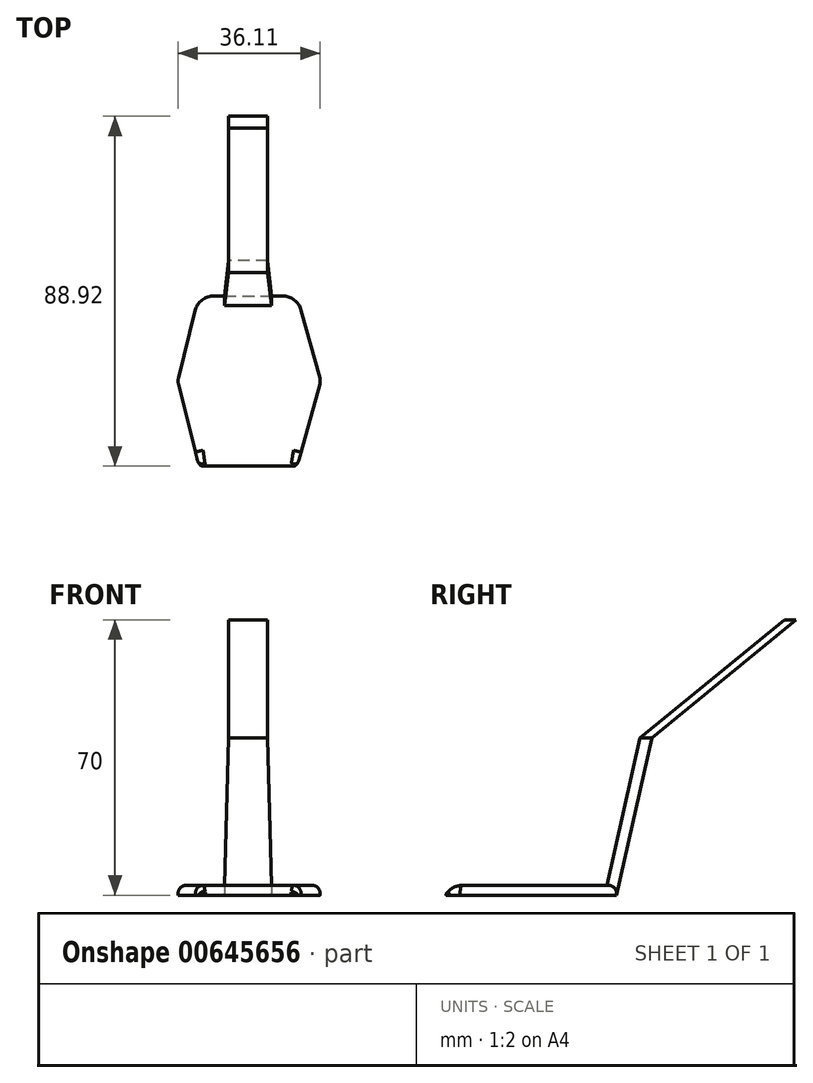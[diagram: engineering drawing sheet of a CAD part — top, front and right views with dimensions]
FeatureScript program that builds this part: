
annotation { "Feature Type Name" : "Feature", "Feature Type Description" : "" }
export const myFeature = defineFeature(function(context is Context, id is Id, definition is map)
    precondition{}
    {
        {
            var Q0;
            Q0=qCreatedBy(makeId("Top.planeOp"),FACE);
            var sketch = newSketch(context, id + "F0", { "sketchPlane" : qUnion([Q0])});
            skLineSegment(sketch, "E0.0", {"start": v(-12.5, 21.65) * mm, "end": v(12.5, 21.65) * mm});
            skLineSegment(sketch, "E0.1", {"start": v(12.5, 21.65) * mm, "end": v(18.43, 0) * mm});
            skLineSegment(sketch, "E0.2", {"start": v(18.43, 0) * mm, "end": v(12.5, -21.65) * mm});
            skLineSegment(sketch, "E0.3", {"start": v(12.5, -21.65) * mm, "end": v(-12.5, -21.65) * mm});
            skLineSegment(sketch, "E0.4", {"start": v(-12.5, -21.65) * mm, "end": v(-17.89, 0) * mm});
            skLineSegment(sketch, "E0.5", {"start": v(-17.89, 0) * mm, "end": v(-12.5, 21.65) * mm});
            skPoint(sketch, "E0.0.midPoint", {"position": v(0, 21.65) * mm});
            skSolve(sketch);
        }
        {
            var Q0;
            Q0 = qSketchRegion(id + "F0", true);
            extrude(context, id + "F1", {"entities" : qUnion([Q0]), "depth" : 2.5 * mm, "offsetDistance" : 25 * mm});
        }
        {
            var Q0;
            Q0=qCreatedBy(makeId("Top.planeOp"),FACE);
            cPlane(context, id + "F2", {"entities" : qUnion([Q0]), "cplaneType" : CPlaneType.OFFSET, "offset" : 40 * mm, "width" : 150 * mm, "height" : 150 * mm});
        }
        {
            var Q0;
            Q0=qCreatedBy(id+"F2.planeOp",FACE);
            var sketch = newSketch(context, id + "F3", { "sketchPlane" : qUnion([Q0])});
            skLineSegment(sketch, "E1.bottom", {"start": v(5, 27.57) * mm, "end": v(-5, 27.57) * mm});
            skLineSegment(sketch, "E1.top", {"start": v(5, 30.57) * mm, "end": v(-5, 30.57) * mm});
            skLineSegment(sketch, "E1.left", {"start": v(5, 27.57) * mm, "end": v(5, 30.57) * mm});
            skLineSegment(sketch, "E1.right", {"start": v(-5, 27.57) * mm, "end": v(-5, 30.57) * mm});
            skPoint(sketch, "E1.middle", {"position": v(0, 29.07) * mm});
            skSolve(sketch);
        }
        {
            var Q0;
            Q0=makeQuery(id+"F1.opExtrude","CAP_FACE",FACE,{"disambiguationData":[OSD([sQuery(id+"F0.wireOp",EDGE,"E0.0"),sQuery(id+"F0.wireOp",EDGE,"E0.1"),sQuery(id+"F0.wireOp",EDGE,"E0.2"),sQuery(id+"F0.wireOp",EDGE,"E0.3"),sQuery(id+"F0.wireOp",EDGE,"E0.4"),sQuery(id+"F0.wireOp",EDGE,"E0.5")])],"isStart":true});
            var sketch = newSketch(context, id + "F4", { "sketchPlane" : qUnion([Q0])});
            skLineSegment(sketch, "E2.bottom", {"start": v(6, -21.65) * mm, "end": v(-6, -21.65) * mm});
            skLineSegment(sketch, "E2.top", {"start": v(6, -18.65) * mm, "end": v(-6, -18.65) * mm});
            skLineSegment(sketch, "E2.left", {"start": v(6, -21.65) * mm, "end": v(6, -18.65) * mm});
            skLineSegment(sketch, "E2.right", {"start": v(-6, -21.65) * mm, "end": v(-6, -18.65) * mm});
            skPoint(sketch, "E2.middle", {"position": v(0, -20.15) * mm});
            skSolve(sketch);
        }
        {
            var Q1;
            Q1=makeQuery(id+"F4.imprint","IMPRINT",FACE,{"disambiguationData":[TD([[makeQuery(id+"F4.imprint","IMPRINT",EDGE,{"derivedFrom":sQuery(id+"F4.wireOp",EDGE,"E2.bottom")}),1.0]])]});
            var Q2;
            Q2=makeQuery(id+"F3.imprint","IMPRINT",FACE,{"disambiguationData":[TD([[makeQuery(id+"F3.imprint","IMPRINT",EDGE,{"derivedFrom":sQuery(id+"F3.wireOp",EDGE,"E1.bottom")}),-1.0]])]});
            loft(context, id + "F5", {"operationType" : NewBodyOperationType.ADD, "sheetProfilesArray" : [{ "sheetProfileEntities" : qUnion([Q1]) }, { "sheetProfileEntities" : qUnion([Q2]) }]});
        }
        {
            var Q0;
            Q0=qCreatedBy(id+"F2.planeOp",FACE);
            cPlane(context, id + "F6", {"entities" : qUnion([Q0]), "cplaneType" : CPlaneType.OFFSET, "offset" : 30 * mm, "width" : 150 * mm, "height" : 150 * mm});
        }
        {
            var Q0;
            Q0=qCreatedBy(id+"F6.planeOp",FACE);
            var sketch = newSketch(context, id + "F7", { "sketchPlane" : qUnion([Q0])});
            skLineSegment(sketch, "E3.bottom", {"start": v(5, 64.27) * mm, "end": v(-5, 64.27) * mm});
            skLineSegment(sketch, "E3.top", {"start": v(5, 67.27) * mm, "end": v(-5, 67.27) * mm});
            skLineSegment(sketch, "E3.left", {"start": v(5, 64.27) * mm, "end": v(5, 67.27) * mm});
            skLineSegment(sketch, "E3.right", {"start": v(-5, 64.27) * mm, "end": v(-5, 67.27) * mm});
            skPoint(sketch, "E3.middle", {"position": v(0, 65.77) * mm});
            skSolve(sketch);
        }
        {
            var Q1;
            Q1=makeQuery(id+"F5.opLoft","CAP_FACE",FACE,{"disambiguationData":[OSD([makeQuery(id+"F3.imprint","IMPRINT",FACE,{"disambiguationData":[TD([[makeQuery(id+"F3.imprint","IMPRINT",EDGE,{"derivedFrom":sQuery(id+"F3.wireOp",EDGE,"E1.bottom")}),-1.0]])]})])],"isStart":true});
            var Q2;
            Q2=makeQuery(id+"F7.imprint","IMPRINT",FACE,{"disambiguationData":[TD([[makeQuery(id+"F7.imprint","IMPRINT",EDGE,{"derivedFrom":sQuery(id+"F7.wireOp",EDGE,"E3.bottom")}),-1.0]])]});
            loft(context, id + "F8", {"operationType" : NewBodyOperationType.ADD, "sheetProfilesArray" : [{ "sheetProfileEntities" : qUnion([Q1]) }, { "sheetProfileEntities" : qUnion([Q2]) }]});
        }
        {
            var Q0;
            Q0=makeQuery(id+"F1.opExtrude","CAP_EDGE",EDGE,{"disambiguationData":[OSD([sQuery(id+"F0.wireOp",EDGE,"E0.3")])],"isStart":false});
            chamfer(context, id + "F9", {"entities" : qUnion([Q0]), "width" : 2 * mm, "tangentPropagation" : true});
        }
        {
            var Q0;
            {var subQ0=sQuery(id+"F0.wireOp",EDGE,"E0.3");Q0=makeQuery(id+"F9.opChamfer","BLEND_EDGE",EDGE,{"blendedFrom":[makeQuery(id+"F1.opExtrude","CAP_EDGE",EDGE,{"disambiguationData":[OSD([subQ0])],"isStart":false}),makeQuery(id+"F1.opExtrude","CAP_FACE",FACE,{"disambiguationData":[OSD([sQuery(id+"F0.wireOp",EDGE,"E0.0"),sQuery(id+"F0.wireOp",EDGE,"E0.1"),sQuery(id+"F0.wireOp",EDGE,"E0.2"),subQ0,sQuery(id+"F0.wireOp",EDGE,"E0.4"),sQuery(id+"F0.wireOp",EDGE,"E0.5")])],"isStart":false})],"blendedInto":[makeQuery(id+"F1.opExtrude","CAP_FACE",FACE,{"disambiguationData":[OSD([sQuery(id+"F0.wireOp",EDGE,"E0.0"),sQuery(id+"F0.wireOp",EDGE,"E0.1"),sQuery(id+"F0.wireOp",EDGE,"E0.2"),subQ0,sQuery(id+"F0.wireOp",EDGE,"E0.4"),sQuery(id+"F0.wireOp",EDGE,"E0.5")])],"isStart":false})]});}
            fillet(context, id + "F10", {"entities" : qUnion([Q0]), "radius" : 5 * mm, "tangentPropagation" : true, "allowEdgeOverflow" : false});
        }
        {
            var Q0;
            Q0=makeQuery(id+"F1.opExtrude","SWEPT_EDGE",EDGE,{"disambiguationData":[OSD([sQuery(id+"F0.wireOp",EDGE,"E0.0"),sQuery(id+"F0.wireOp",EDGE,"E0.5")])]});
            var Q1;
            Q1=makeQuery(id+"F1.opExtrude","SWEPT_EDGE",EDGE,{"disambiguationData":[OSD([sQuery(id+"F0.wireOp",EDGE,"E0.0"),sQuery(id+"F0.wireOp",EDGE,"E0.1")])]});
            fillet(context, id + "F11", {"entities" : qUnion([Q0, Q1]), "radius" : 5 * mm, "tangentPropagation" : true, "allowEdgeOverflow" : false});
        }
        {
            var Q0;
            Q0=makeQuery(id+"F1.opExtrude","SWEPT_EDGE",EDGE,{"disambiguationData":[OSD([sQuery(id+"F0.wireOp",EDGE,"E0.4"),sQuery(id+"F0.wireOp",EDGE,"E0.5")])]});
            var Q1;
            Q1=makeQuery(id+"F1.opExtrude","SWEPT_EDGE",EDGE,{"disambiguationData":[OSD([sQuery(id+"F0.wireOp",EDGE,"E0.1"),sQuery(id+"F0.wireOp",EDGE,"E0.2")])]});
            fillet(context, id + "F12", {"entities" : qUnion([Q0, Q1]), "radius" : 3 * mm, "tangentPropagation" : true, "allowEdgeOverflow" : false});
        }
        {
            var Q0;
            Q0=makeQuery(id+"F1.opExtrude","CAP_EDGE",EDGE,{"disambiguationData":[OSD([sQuery(id+"F0.wireOp",EDGE,"E0.2")])],"isStart":false});
            var Q1;
            Q1=makeQuery(id+"F1.opExtrude","CAP_EDGE",EDGE,{"disambiguationData":[OSD([sQuery(id+"F0.wireOp",EDGE,"E0.1")])],"isStart":false});
            var Q2;
            Q2=makeQuery(id+"F1.opExtrude","CAP_EDGE",EDGE,{"disambiguationData":[OSD([sQuery(id+"F0.wireOp",EDGE,"E0.4")])],"isStart":false});
            var Q3;
            Q3=makeQuery(id+"F1.opExtrude","CAP_EDGE",EDGE,{"disambiguationData":[OSD([sQuery(id+"F0.wireOp",EDGE,"E0.5")])],"isStart":false});
            fillet(context, id + "F13", {"entities" : qUnion([Q0, Q1, Q2, Q3]), "radius" : 2 * mm, "tangentPropagation" : true, "allowEdgeOverflow" : false});
        }
        {
            var Q0;
            {var subQ0=sQuery(id+"F0.wireOp",EDGE,"E0.3");Q0=makeQuery(id+"F9.opChamfer","BLEND_EDGE",EDGE,{"blendedFrom":[makeQuery(id+"F1.opExtrude","CAP_EDGE",EDGE,{"disambiguationData":[OSD([subQ0])],"isStart":false}),makeQuery(id+"F1.opExtrude","SWEPT_FACE",FACE,{"disambiguationData":[OSD([subQ0])]})],"blendedInto":[makeQuery(id+"F1.opExtrude","SWEPT_FACE",FACE,{"disambiguationData":[OSD([subQ0])]})]});}
            fillet(context, id + "F14", {"entities" : qUnion([Q0]), "radius" : 1 * mm, "tangentPropagation" : true, "allowEdgeOverflow" : false});
        }
    });
